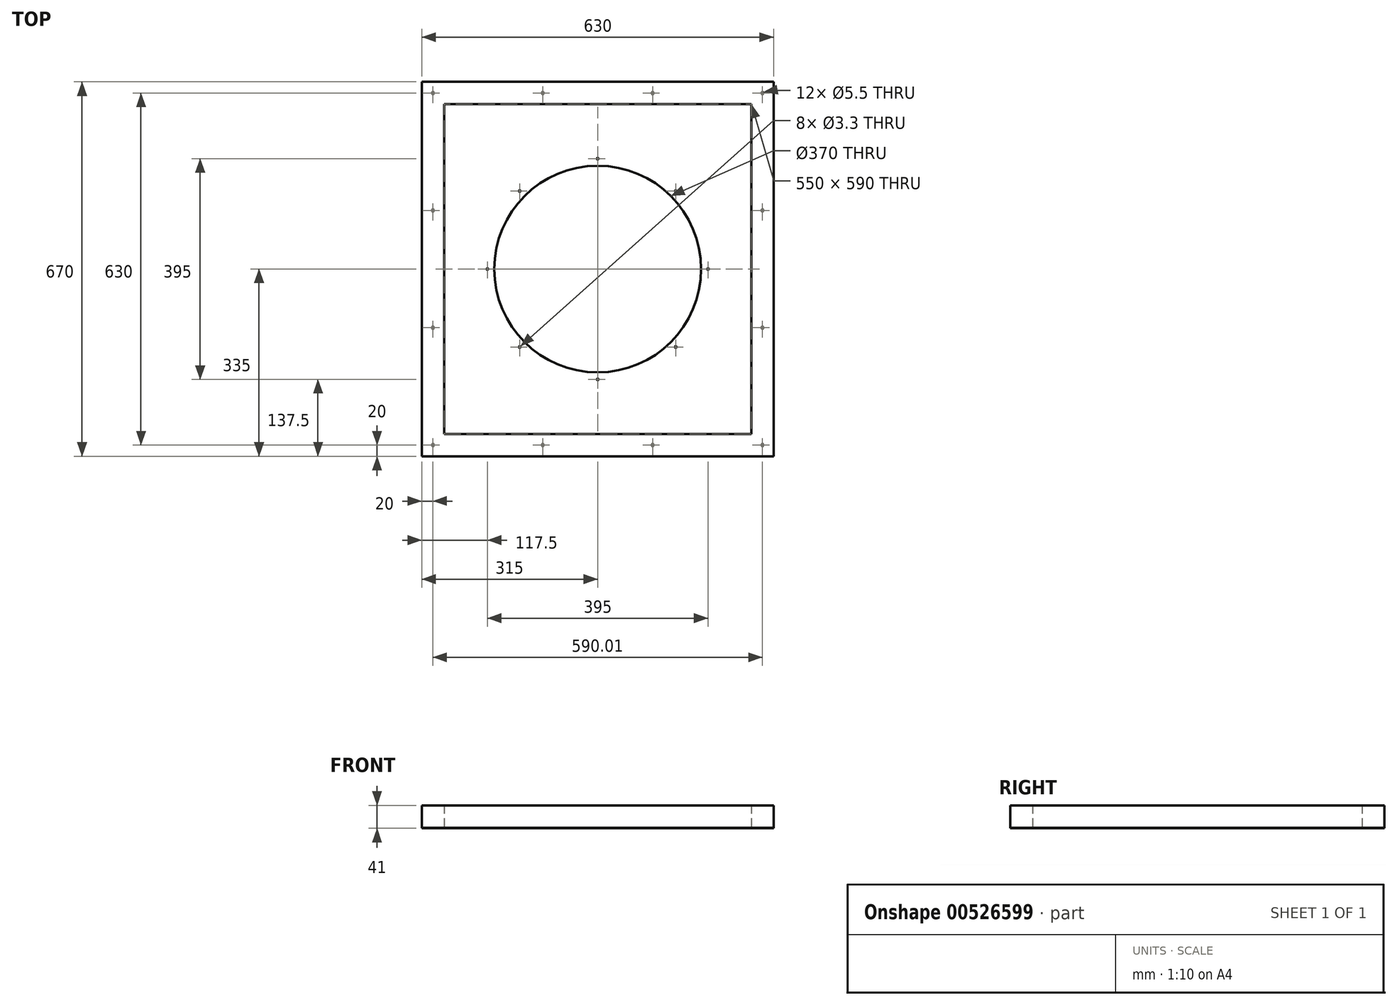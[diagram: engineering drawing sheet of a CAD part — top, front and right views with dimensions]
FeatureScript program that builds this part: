
annotation { "Feature Type Name" : "Feature", "Feature Type Description" : "" }
export const myFeature = defineFeature(function(context is Context, id is Id, definition is map)
    precondition{}
    {
        {
            var Q0;
            Q0=qCreatedBy(makeId("Top.planeOp"),FACE);
            var sketch = newSketch(context, id + "F0", { "sketchPlane" : qUnion([Q0])});
            skCircle(sketch, "E0", {"center": v(0, 0) * mm, "radius": 185 * mm});
            skLineSegment(sketch, "E1.top", {"start": v(-24.8, 295) * mm, "end": v(275, 295) * mm});
            skLineSegment(sketch, "E2.top", {"start": v(0, -335) * mm, "end": v(-275, -335) * mm});
            skLineSegment(sketch, "E3.bottom", {"start": v(-275, -335) * mm, "end": v(275, -335) * mm});
            skLineSegment(sketch, "E3.top", {"start": v(-275, 295) * mm, "end": v(275, 295) * mm});
            skLineSegment(sketch, "E3.left", {"start": v(-275, -335) * mm, "end": v(-275, 295) * mm});
            skLineSegment(sketch, "E3.right", {"start": v(275, -335) * mm, "end": v(275, 295) * mm});
            skLineSegment(sketch, "E4.bottom", {"start": v(-315, -335) * mm, "end": v(-275, -335) * mm});
            skLineSegment(sketch, "E4.top", {"start": v(-315, 335) * mm, "end": v(-275, 335) * mm});
            skLineSegment(sketch, "E4.left", {"start": v(-315, -335) * mm, "end": v(-315, 335) * mm});
            skLineSegment(sketch, "E4.right", {"start": v(-275, -335) * mm, "end": v(-275, 335) * mm});
            skLineSegment(sketch, "E5.bottom", {"start": v(275, 295) * mm, "end": v(-275, 295) * mm});
            skLineSegment(sketch, "E5.top", {"start": v(275, 335) * mm, "end": v(-275, 335) * mm});
            skLineSegment(sketch, "E5.left", {"start": v(275, 295) * mm, "end": v(275, 335) * mm});
            skLineSegment(sketch, "E5.right", {"start": v(-275, 295) * mm, "end": v(-275, 335) * mm});
            skLineSegment(sketch, "E6.bottom", {"start": v(275, -335) * mm, "end": v(-275, -335) * mm});
            skLineSegment(sketch, "E6.left", {"start": v(275, -325) * mm, "end": v(275, -335) * mm});
            skLineSegment(sketch, "E6.right", {"start": v(-275, -335) * mm, "end": v(-275, -335) * mm});
            skCircle(sketch, "E7", {"center": v(0, 0) * mm, "radius": 197.5 * mm, "construction": true});
            skPoint(sketch, "E8", {"position": v(0, 197.5) * mm});
            skPoint(sketch, "E9", {"position": v(197.5, 0) * mm});
            skPoint(sketch, "E10", {"position": v(0, -197.5) * mm});
            skPoint(sketch, "E11", {"position": v(-197.5, 0) * mm});
            skPoint(sketch, "E12", {"position": v(-139.65, 139.65) * mm});
            skPoint(sketch, "E13", {"position": v(139.65, 139.65) * mm});
            skPoint(sketch, "E14", {"position": v(139.65, -139.65) * mm});
            skPoint(sketch, "E15", {"position": v(-139.65, -139.65) * mm});
            skPoint(sketch, "E16", {"position": v(-295, 315) * mm});
            skPoint(sketch, "E17.1.0.0", {"position": v(-98.33, 315) * mm});
            skPoint(sketch, "E17.2.0.0", {"position": v(98.34, 315) * mm});
            skPoint(sketch, "E17.3.0.0", {"position": v(295, 315) * mm});
            skLineSegment(sketch, "E17.direction1", {"start": v(-295, 315) * mm, "end": v(-98.33, 315) * mm, "construction": true});
            skPoint(sketch, "E18.0.1.0", {"position": v(-295, 105) * mm});
            skPoint(sketch, "E18.0.2.0", {"position": v(-295, -105) * mm});
            skPoint(sketch, "E18.0.3.0", {"position": v(-295, -315) * mm});
            skLineSegment(sketch, "E18.direction1", {"start": v(-295, 315) * mm, "end": v(-167.8, 315) * mm, "construction": true});
            skLineSegment(sketch, "E18.direction2", {"start": v(-295, 315) * mm, "end": v(-295, 105) * mm, "construction": true});
            skPoint(sketch, "E19.1.0.0", {"position": v(-98.33, -315) * mm});
            skLineSegment(sketch, "E19.direction1", {"start": v(-295, -315) * mm, "end": v(-98.33, -315) * mm, "construction": true});
            skCircle(sketch, "E20", {"center": v(0, 0) * mm, "radius": 165 * mm, "construction": true});
            skPoint(sketch, "E21", {"position": v(0, 165) * mm});
            skPoint(sketch, "E22", {"position": v(-165, 0) * mm});
            skPoint(sketch, "E23", {"position": v(0, -165) * mm});
            skPoint(sketch, "E24", {"position": v(165, 0) * mm});
            skPoint(sketch, "E25", {"position": v(-116.67, -116.67) * mm});
            skPoint(sketch, "E26", {"position": v(116.67, -116.67) * mm});
            skPoint(sketch, "E27", {"position": v(116.67, 116.67) * mm});
            skPoint(sketch, "E28", {"position": v(-116.67, 116.67) * mm});
            skLineSegment(sketch, "E29.bottom", {"start": v(275, 335) * mm, "end": v(315, 335) * mm});
            skLineSegment(sketch, "E29.top", {"start": v(275, -335) * mm, "end": v(315, -335) * mm});
            skLineSegment(sketch, "E29.left", {"start": v(275, 335) * mm, "end": v(275, -335) * mm});
            skLineSegment(sketch, "E29.right", {"start": v(315, 335) * mm, "end": v(315, -335) * mm});
            skLineSegment(sketch, "E30.top", {"start": v(275, -295) * mm, "end": v(-275, -295) * mm});
            skLineSegment(sketch, "E30.left", {"start": v(275, -335) * mm, "end": v(275, -295) * mm});
            skLineSegment(sketch, "E30.right", {"start": v(-275, -335) * mm, "end": v(-275, -295) * mm});
            skPoint(sketch, "E31.0.2.0", {"position": v(98.34, -315) * mm});
            skPoint(sketch, "E32.0.1.0", {"position": v(295, 105) * mm});
            skPoint(sketch, "E32.0.2.0", {"position": v(295, -105) * mm});
            skPoint(sketch, "E32.0.3.0", {"position": v(295, -315) * mm});
            skLineSegment(sketch, "E32.direction1", {"start": v(295, 315) * mm, "end": v(320, 315) * mm, "construction": true});
            skLineSegment(sketch, "E32.direction2", {"start": v(295, 315) * mm, "end": v(295, 105) * mm, "construction": true});
            skSolve(sketch);
        }
        {
            var Q0;
            Q0=makeQuery(id+"F0.imprint","IMPRINT",FACE,{"disambiguationData":[TD([[makeQuery(id+"F0.imprint","IMPRINT",EDGE,{"derivedFrom":sQuery(id+"F0.wireOp",EDGE,"E4.bottom")}),1.0]])]});
            var Q1;
            {var subQ5=sQuery(id+"F0.wireOp",EDGE,"E5.top");Q1=makeQuery(id+"F0.imprint","IMPRINT",FACE,{"disambiguationData":[TD([[makeQuery(id+"F0.imprint","IMPRINT",EDGE,{"derivedFrom":subQ5}),1.0]])]});}
            var Q2;
            {var subQ3=sQuery(id+"F0.wireOp",EDGE,"bYoLXCcc-PKzl-f6ig-5LKm-x8JjXDVLTTpz.bottom");Q2=makeQuery(id+"F0.imprint","IMPRINT",FACE,{"disambiguationData":[TD([[makeQuery(id+"F0.imprint","IMPRINT",EDGE,{"derivedFrom":subQ3}),-1.0]])]});}
            var Q3;
            {var subQ6=sQuery(id+"F0.wireOp",EDGE,"E6.top");Q3=makeQuery(id+"F0.imprint","IMPRINT",FACE,{"disambiguationData":[TD([[makeQuery(id+"F0.imprint","IMPRINT",EDGE,{"derivedFrom":subQ6}),-1.0]])]});}
            var Q4;
            {var subQ3=sQuery(id+"F0.wireOp",EDGE,"E29.bottom");Q4=makeQuery(id+"F0.imprint","IMPRINT",FACE,{"disambiguationData":[TD([[makeQuery(id+"F0.imprint","IMPRINT",EDGE,{"derivedFrom":subQ3}),-1.0]])]});}
            var Q5;
            Q5=makeQuery(id+"F0.imprint","IMPRINT",FACE,{"disambiguationData":[TD([[makeQuery(id+"F0.imprint","IMPRINT",EDGE,{"derivedFrom":sQuery(id+"F0.wireOp",EDGE,"E30.top")}),1.0]])]});
            extrude(context, id + "F1", {"entities" : qUnion([Q0, Q1, Q2, Q3, Q4, Q5]), "depth" : 40 * mm, "offsetDistance" : 25 * mm});
        }
        {
            var Q0;
            Q0=makeQuery(id+"F0.imprint","IMPRINT",FACE,{"disambiguationData":[TD([[makeQuery(id+"F0.imprint","IMPRINT",EDGE,{"derivedFrom":sQuery(id+"F0.wireOp",EDGE,"E0")}),-1.0]])]});
            var Q1;
            {var subQ1=sQuery(id+"F0.wireOp",EDGE,"E5.top");Q1=makeQuery(id+"F0.imprint","IMPRINT",FACE,{"disambiguationData":[TD([[makeQuery(id+"F0.imprint","IMPRINT",EDGE,{"derivedFrom":subQ1}),1.0]])]});}
            var Q2;
            {var subQ3=sQuery(id+"F0.wireOp",EDGE,"E29.bottom");Q2=makeQuery(id+"F0.imprint","IMPRINT",FACE,{"disambiguationData":[TD([[makeQuery(id+"F0.imprint","IMPRINT",EDGE,{"derivedFrom":subQ3}),-1.0]])]});}
            var Q3;
            Q3=makeQuery(id+"F0.imprint","IMPRINT",FACE,{"disambiguationData":[TD([[makeQuery(id+"F0.imprint","IMPRINT",EDGE,{"derivedFrom":sQuery(id+"F0.wireOp",EDGE,"E4.bottom")}),1.0]])]});
            var Q4;
            Q4=makeQuery(id+"F0.imprint","IMPRINT",FACE,{"disambiguationData":[TD([[makeQuery(id+"F0.imprint","IMPRINT",EDGE,{"derivedFrom":sQuery(id+"F0.wireOp",EDGE,"E30.top")}),1.0]])]});
            extrude(context, id + "F2", {"entities" : qUnion([Q0, Q1, Q2, Q3, Q4]), "oppositeDirection" : true, "depth" : 1 * mm, "offsetDistance" : 25 * mm});
        }
        {
            var Q0;
            Q0=sQuery(id+"F0.wireOp",VERTEX,"E8");
            var Q1;
            Q1=sQuery(id+"F0.wireOp",VERTEX,"E13");
            var Q2;
            Q2=sQuery(id+"F0.wireOp",VERTEX,"E9");
            var Q3;
            Q3=sQuery(id+"F0.wireOp",VERTEX,"E14");
            var Q4;
            Q4=sQuery(id+"F0.wireOp",VERTEX,"E10");
            var Q5;
            Q5=sQuery(id+"F0.wireOp",VERTEX,"E15");
            var Q6;
            Q6=sQuery(id+"F0.wireOp",VERTEX,"E12");
            var Q7;
            Q7=sQuery(id+"F0.wireOp",VERTEX,"E11");
            var Q8;
            Q8=makeQuery(id+"F2.opExtrude","SWEPT_BODY",BODY,{"disambiguationData":[OSD([sQuery(id+"F0.wireOp",EDGE,"E0"),sQuery(id+"F0.wireOp",EDGE,"E4.bottom"),sQuery(id+"F0.wireOp",EDGE,"E4.top"),sQuery(id+"F0.wireOp",EDGE,"E4.left"),sQuery(id+"F0.wireOp",EDGE,"E5.top"),sQuery(id+"F0.wireOp",EDGE,"E6.top"),sQuery(id+"F0.wireOp",EDGE,"bYoLXCcc-PKzl-f6ig-5LKm-x8JjXDVLTTpz.bottom"),sQuery(id+"F0.wireOp",EDGE,"bYoLXCcc-PKzl-f6ig-5LKm-x8JjXDVLTTpz.top"),sQuery(id+"F0.wireOp",EDGE,"bYoLXCcc-PKzl-f6ig-5LKm-x8JjXDVLTTpz.right")])]});
            hole(context, id + "F3", {"style" : HoleStyle.SIMPLE, "endStyle" : HoleEndStyle.BLIND, "standardTappedOrClearance" : lookupTablePath({ "standard" : "ISO", "fit" : "Normal", "size" : "M3", "type" : "Clearance" }), "standardBlindInLast" : lookupTablePath({ "fit" : "Standard", "standard" : "ISO", "size" : "M3", "type" : "Clearance" }), "holeDiameter" : 3.3 * mm, "majorDiameter" : 5 * mm, "holeDepth" : 50 * mm, "isTappedThrough" : true, "tappedDepth" : 12 * mm, "tapClearance" : 3, "locations" : qUnion([Q0, Q1, Q2, Q3, Q4, Q5, Q6, Q7]), "scope" : qUnion([Q8]), "startStyle" : HoleStartStyle.PART});
        }
        {
            var Q0;
            Q0=sQuery(id+"F0.wireOp",VERTEX,"E32.0.3.0");
            var Q1;
            Q1=sQuery(id+"F0.wireOp",VERTEX,"E32.0.2.0");
            var Q2;
            Q2=sQuery(id+"F0.wireOp",VERTEX,"E32.0.1.0");
            var Q3;
            Q3=sQuery(id+"F0.wireOp",VERTEX,"E17.3.0.0");
            var Q4;
            Q4=sQuery(id+"F0.wireOp",VERTEX,"E17.2.0.0");
            var Q5;
            Q5=sQuery(id+"F0.wireOp",VERTEX,"E17.1.0.0");
            var Q6;
            Q6=sQuery(id+"F0.wireOp",VERTEX,"E16");
            var Q7;
            Q7=sQuery(id+"F0.wireOp",VERTEX,"E18.0.1.0");
            var Q8;
            Q8=sQuery(id+"F0.wireOp",VERTEX,"E18.0.2.0");
            var Q9;
            Q9=sQuery(id+"F0.wireOp",VERTEX,"E18.0.3.0");
            var Q10;
            Q10=sQuery(id+"F0.wireOp",VERTEX,"E19.1.0.0");
            var Q11;
            Q11=sQuery(id+"F0.wireOp",VERTEX,"E31.0.2.0");
            var Q12;
            Q12=makeQuery(id+"F2.opExtrude","SWEPT_BODY",BODY,{"disambiguationData":[OSD([sQuery(id+"F0.wireOp",EDGE,"E0"),sQuery(id+"F0.wireOp",EDGE,"E4.bottom"),sQuery(id+"F0.wireOp",EDGE,"E4.top"),sQuery(id+"F0.wireOp",EDGE,"E4.left"),sQuery(id+"F0.wireOp",EDGE,"E5.top"),sQuery(id+"F0.wireOp",EDGE,"E6.top"),sQuery(id+"F0.wireOp",EDGE,"bYoLXCcc-PKzl-f6ig-5LKm-x8JjXDVLTTpz.bottom"),sQuery(id+"F0.wireOp",EDGE,"bYoLXCcc-PKzl-f6ig-5LKm-x8JjXDVLTTpz.top"),sQuery(id+"F0.wireOp",EDGE,"bYoLXCcc-PKzl-f6ig-5LKm-x8JjXDVLTTpz.right")])]});
            hole(context, id + "F4", {"style" : HoleStyle.SIMPLE, "endStyle" : HoleEndStyle.THROUGH, "standardTappedOrClearance" : lookupTablePath({ "standard" : "ISO", "fit" : "Normal", "size" : "M5", "type" : "Clearance" }), "standardBlindInLast" : lookupTablePath({ "fit" : "Standard", "standard" : "ISO", "size" : "M5", "type" : "Clearance" }), "holeDiameter" : 5.5 * mm, "majorDiameter" : 5 * mm, "isTappedThrough" : true, "tappedDepth" : 12 * mm, "tapClearance" : 3, "locations" : qUnion([Q0, Q1, Q2, Q3, Q4, Q5, Q6, Q7, Q8, Q9, Q10, Q11]), "scope" : qUnion([Q12]), "startStyle" : HoleStartStyle.PART});
        }
    });
